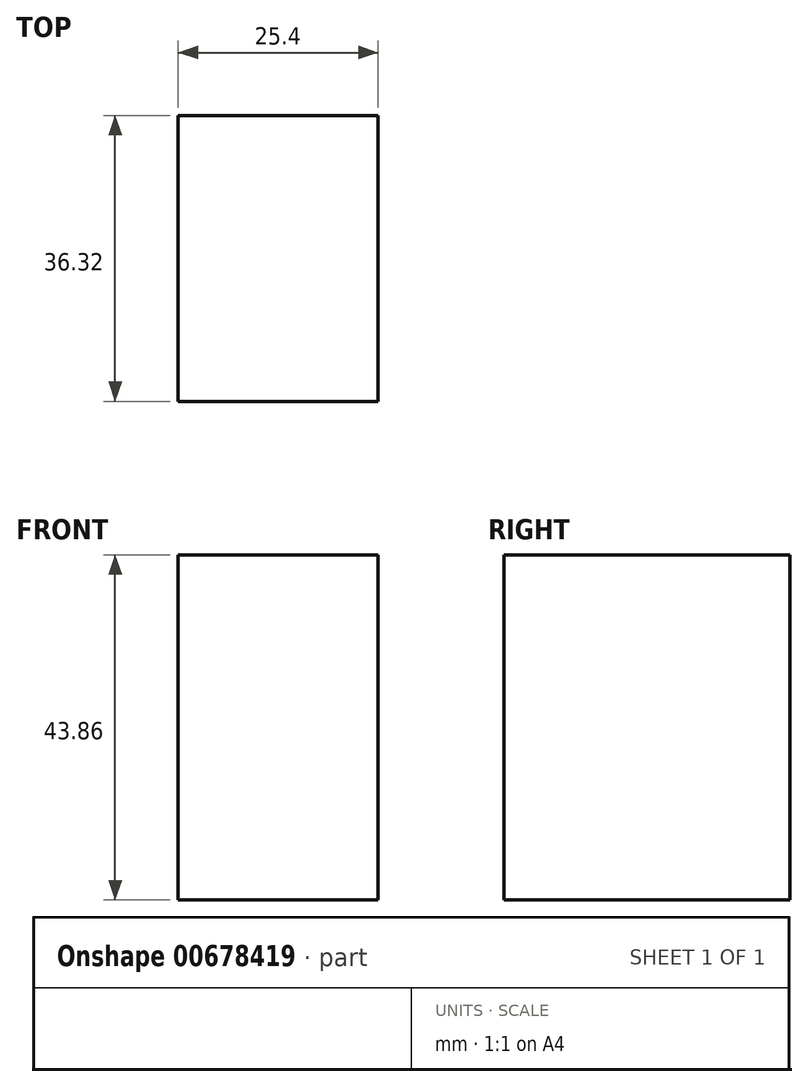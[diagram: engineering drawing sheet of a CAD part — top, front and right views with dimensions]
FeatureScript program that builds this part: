
annotation { "Feature Type Name" : "Feature", "Feature Type Description" : "" }
export const myFeature = defineFeature(function(context is Context, id is Id, definition is map)
    precondition{}
    {
        {
            var Q0;
            Q0=qCreatedBy(makeId("Right.planeOp"),FACE);
            var sketch = newSketch(context, id + "F0", { "sketchPlane" : qUnion([Q0])});
            skLineSegment(sketch, "E0.bottom", {"start": v(0, 0) * mm, "end": v(-36.32, 0) * mm});
            skLineSegment(sketch, "E0.top", {"start": v(0, 43.86) * mm, "end": v(-36.32, 43.86) * mm});
            skLineSegment(sketch, "E0.left", {"start": v(0, 0) * mm, "end": v(0, 43.86) * mm});
            skLineSegment(sketch, "E0.right", {"start": v(-36.32, 0) * mm, "end": v(-36.32, 43.86) * mm});
            skSolve(sketch);
        }
        {
            var Q0;
            Q0 = qSketchRegion(id + "F0", true);
            extrude(context, id + "F1", {"entities" : qUnion([Q0]), "depth" : 25.4 * mm, "offsetDistance" : 25.4 * mm});
        }
    });
